# Revit family: Sofiero-Curved-bench-90-1400-CC
name_source: partatom
category: Furniture
units: mm (PartAtom-declared; Revit-internal decimal feet)

## family parameters
Always vertical = Yes
Cut with Voids When Loaded = No
OmniClass Number = 23.11.27.00
Room Calculation Point = No
Shared = No
Work Plane-Based = No

## types (6) — shared parameters
45° = Yes
BIMobject category = Chairs, Stools & Benches
Description = Sofiero Curved bench Ø 1400
Edition number = 1
IFC Classification = Furniture
Manufacturer = Hags
Manufacturer name = HAGS
Masterformat 2014 Code = 12 50 00
Masterformat 2014 Description = Furniture
OmniClass Code = 23-21 25 19 11 13
OmniClass Description = Benches
Product Guid = 4cffe3b4-27e0-49ff-8427-d568dce6bf65
Product SKU = Sofiero_Curved_bench_O_1400
Product data url = https://bimobject.com
Product name = Sofiero Curved bench Ø 1400
QR code = https://bimobject.com
URL = https://www.hags.com
Uniclass 1.4 Code = JN
Uniclass 1.4 Description = Furniture/Equipment
zero-valued in all types: Default Elevation

## per-type parameters (varying)
| type | 90° | Body material | Construction material | Model | Product url |
| 8073747 Tan / Galv 45 ° | No | Hags - Wood - Tan | Hags - Steel - Galvanized | 8073747 | https://hags.se |
| 8073748 Bark Brown / Black 45 ° | No | Hags - Wood - Bark brown | Hags - Steel - Powder coated - Black | 8073748 | https://hags.se |
| 8073759 Tan / Galv 90 ° | Yes | Hags - Wood - Tan | Hags - Steel - Galvanized | 8073759 | https://hags.se |
| 8073760 Bark Brown / Black 90 ° | Yes | Hags - Wood - Bark brown | Hags - Steel - Powder coated - Black | 8073759 | https://hags.se |
| 8097638 Hardwood / Galvanized | Yes | Hags - Hard Wood | Hags - Steel - Galvanized | 8097638 | https://www.hags.com |
| 8097639 Hardwood / Black | Yes | Hags - Hard Wood | Hags - Steel - Powder coated - Black | 8097639 | https://www.hags.com |

## geometry (parser evidence)
native form markers: Sweep x3
no freeform markers — native parametric forms only
